# Revit family: Lilja 18W
name_source: partatom
category: Lighting Fixtures
units: mm (PartAtom-declared; Revit-internal decimal feet)

## family parameters
Cut with Voids When Loaded = No
Host = Face
Light Source = Yes
OmniClass Number = 23.80.70.11.11
OmniClass Title = General Luminaries, Non Directional
Part Type = Normal
Room Calculation Point = No
Round Connector Dimension = Use Diameter
Shared = No

## types (4) — shared parameters
Beam Angle = 120°
CRI = 80
Casing Color = White
Color Filter = 16777215
Cutout = 208mm
Default Elevation = 1219 mm
Depth = 30mm
Description = Downlight
Dimensions = 224mm x 20mm
Dimmable = Yes
Dimming Lamp Color Temperature Shift = <None>
Directivity = No
Driver = Separate
Housing Material = Aluminium
IP Code = IP44
Lamp = LED
Last Updated = 25.2.2016
Lifetime L70 = 50000h
Manufacturer = Winled Oy Ltd
Model = Lilja 18W
Operating Temperature Range = -20° to +40°C
Tilt Angle = -90.00°
Type Image = Lilja 18W.png
URL = www.winled.fi
Wattage Comments = 18W

## per-type parameters (varying)
| type | Color Temperature | Lumens Output | Photometric Web File | Product Number | Voltage |
| Lilja 18W, Neutral White, 110V - 02XWP996N018R | 4000K | 1337lm | Lilja 18W NV.ies | 02XWP996N018R | 110 V |
| Lilja 18W, Warm White, 230V - 02WP996L018R | 3000K | 1237lm | Lilja 18W LV.ies | 02WP996L018R | 230 V |
| Lilja 18W, Neutral White, 230V - 02WP996N018R | 4000K | 1337lm | Lilja 18W NV.ies | 02WP996N018R | 230 V |
| Lilja 18W, Warm White, 110V - 02XWP996L018R | 3000K | 1237lm | Lilja 18W LV.ies | 02XWP996L018R | 110 V |

## geometry (parser evidence)
native form markers: Sweep x4
no freeform markers — native parametric forms only
